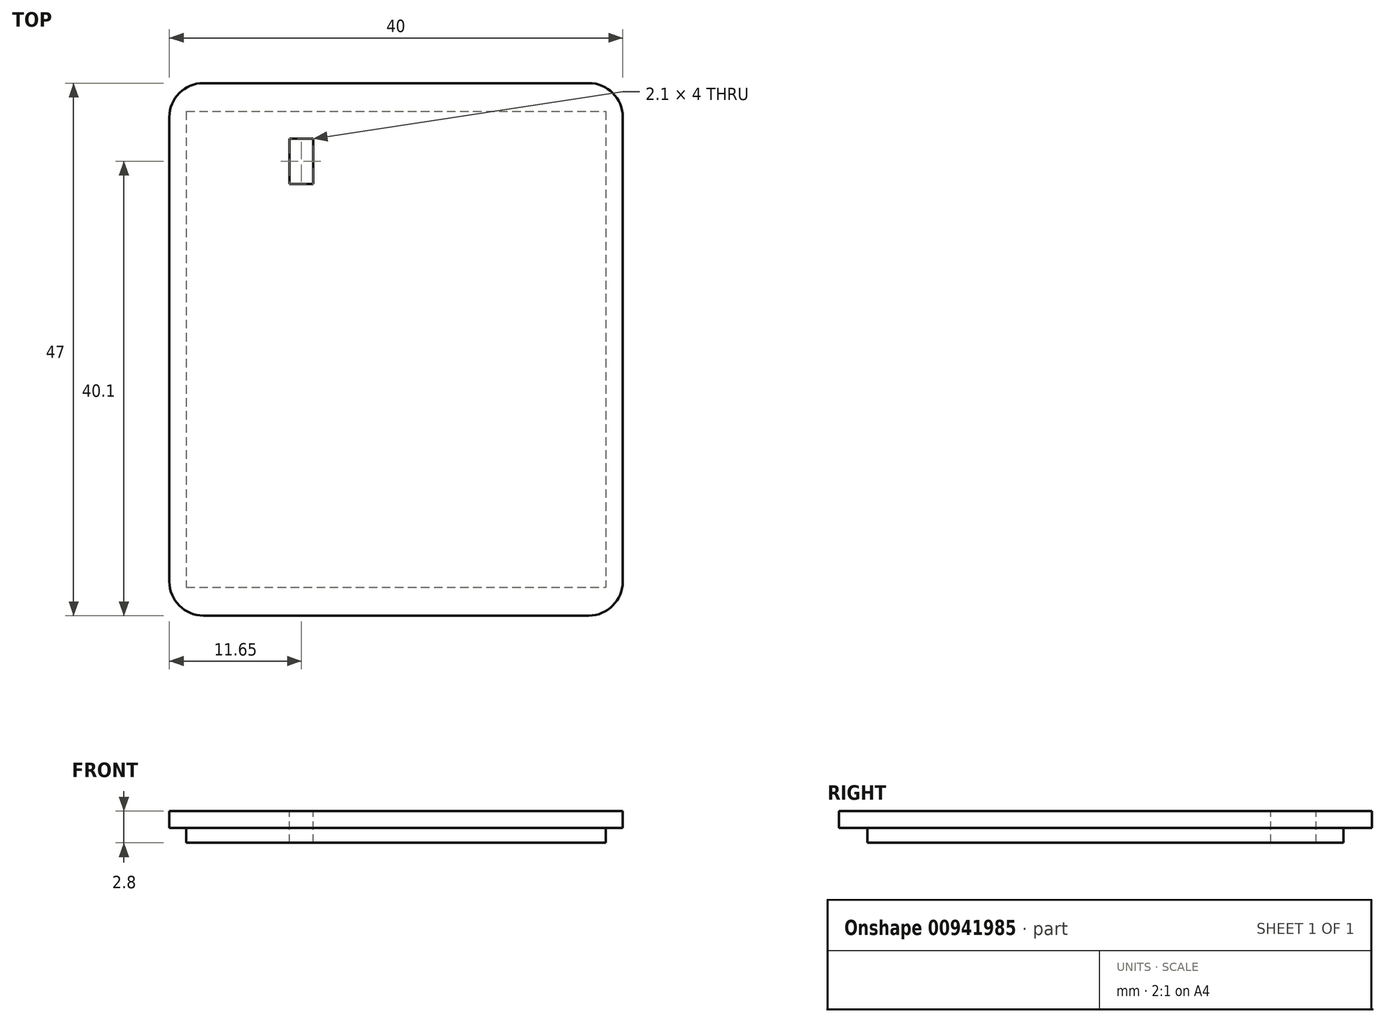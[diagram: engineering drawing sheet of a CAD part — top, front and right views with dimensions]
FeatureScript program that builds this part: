
annotation { "Feature Type Name" : "Feature", "Feature Type Description" : "" }
export const myFeature = defineFeature(function(context is Context, id is Id, definition is map)
    precondition{}
    {
        {
            var Q0;
            Q0=qCreatedBy(makeId("Top.planeOp"),FACE);
            var sketch = newSketch(context, id + "F0", { "sketchPlane" : qUnion([Q0])});
            skLineSegment(sketch, "E0.bottom", {"start": v(-17, 23.5) * mm, "end": v(17, 23.5) * mm});
            skLineSegment(sketch, "E0.top", {"start": v(-17, -23.5) * mm, "end": v(17, -23.5) * mm});
            skLineSegment(sketch, "E0.left", {"start": v(-20, 20.5) * mm, "end": v(-20, -20.5) * mm});
            skLineSegment(sketch, "E0.right", {"start": v(20, 20.5) * mm, "end": v(20, -20.5) * mm});
            skPoint(sketch, "E0.middle", {"position": v(0, 0) * mm});
            skPoint(sketch, "E1.visualSharp", {"position": v(-20, 23.5) * mm});
            skArc(sketch, "E1.filletArc", {"start": v(-17, 23.5) * mm, "mid": v(-19.12, 22.62) * mm, "end": v(-20, 20.5) * mm});
            skPoint(sketch, "E2.visualSharp", {"position": v(20, 23.5) * mm});
            skArc(sketch, "E2.filletArc", {"start": v(20, 20.5) * mm, "mid": v(19.12, 22.62) * mm, "end": v(17, 23.5) * mm});
            skPoint(sketch, "E3.visualSharp", {"position": v(20, -23.5) * mm});
            skArc(sketch, "E3.filletArc", {"start": v(17, -23.5) * mm, "mid": v(19.12, -22.62) * mm, "end": v(20, -20.5) * mm});
            skPoint(sketch, "E4.visualSharp", {"position": v(-20, -23.5) * mm});
            skArc(sketch, "E4.filletArc", {"start": v(-20, -20.5) * mm, "mid": v(-19.12, -22.62) * mm, "end": v(-17, -23.5) * mm});
            skSolve(sketch);
        }
        {
            var Q0;
            Q0 = qSketchRegion(id + "F0", true);
            extrude(context, id + "F1", {"entities" : qUnion([Q0]), "depth" : 1.5 * mm, "offsetDistance" : 25 * mm});
        }
        {
            var Q0;
            Q0=qCreatedBy(makeId("Top.planeOp"),FACE);
            var sketch = newSketch(context, id + "F2", { "sketchPlane" : qUnion([Q0])});
            skLineSegment(sketch, "E5.bottom", {"start": v(-18.5, 21) * mm, "end": v(18.5, 21) * mm});
            skLineSegment(sketch, "E5.top", {"start": v(-18.5, -21) * mm, "end": v(18.5, -21) * mm});
            skLineSegment(sketch, "E5.left", {"start": v(-18.5, 21) * mm, "end": v(-18.5, -21) * mm});
            skLineSegment(sketch, "E5.right", {"start": v(18.5, 21) * mm, "end": v(18.5, -21) * mm});
            skPoint(sketch, "E5.middle", {"position": v(0, 0) * mm});
            skSolve(sketch);
        }
        {
            var Q0;
            Q0 = qSketchRegion(id + "F2", true);
            extrude(context, id + "F3", {"entities" : qUnion([Q0]), "operationType" : NewBodyOperationType.ADD, "oppositeDirection" : true, "depth" : 1.3 * mm, "offsetDistance" : 25 * mm});
        }
        {
            var Q0;
            Q0=qCreatedBy(makeId("Top.planeOp"),FACE);
            var sketch = newSketch(context, id + "F4", { "sketchPlane" : qUnion([Q0])});
            skLineSegment(sketch, "E6.bottom", {"start": v(-9.4, 18.6) * mm, "end": v(-7.3, 18.6) * mm});
            skLineSegment(sketch, "E6.top", {"start": v(-9.4, 14.6) * mm, "end": v(-7.3, 14.6) * mm});
            skLineSegment(sketch, "E6.left", {"start": v(-9.4, 18.6) * mm, "end": v(-9.4, 14.6) * mm});
            skLineSegment(sketch, "E6.right", {"start": v(-7.3, 18.6) * mm, "end": v(-7.3, 14.6) * mm});
            skSolve(sketch);
        }
        {
            var Q0;
            Q0 = qSketchRegion(id + "F4", true);
            extrude(context, id + "F5", {"entities" : qUnion([Q0]), "operationType" : NewBodyOperationType.REMOVE, "endBound" : BoundingType.SYMMETRIC, "oppositeDirection" : true, "depth" : 10.1 * mm, "offsetDistance" : 25 * mm});
        }
    });
